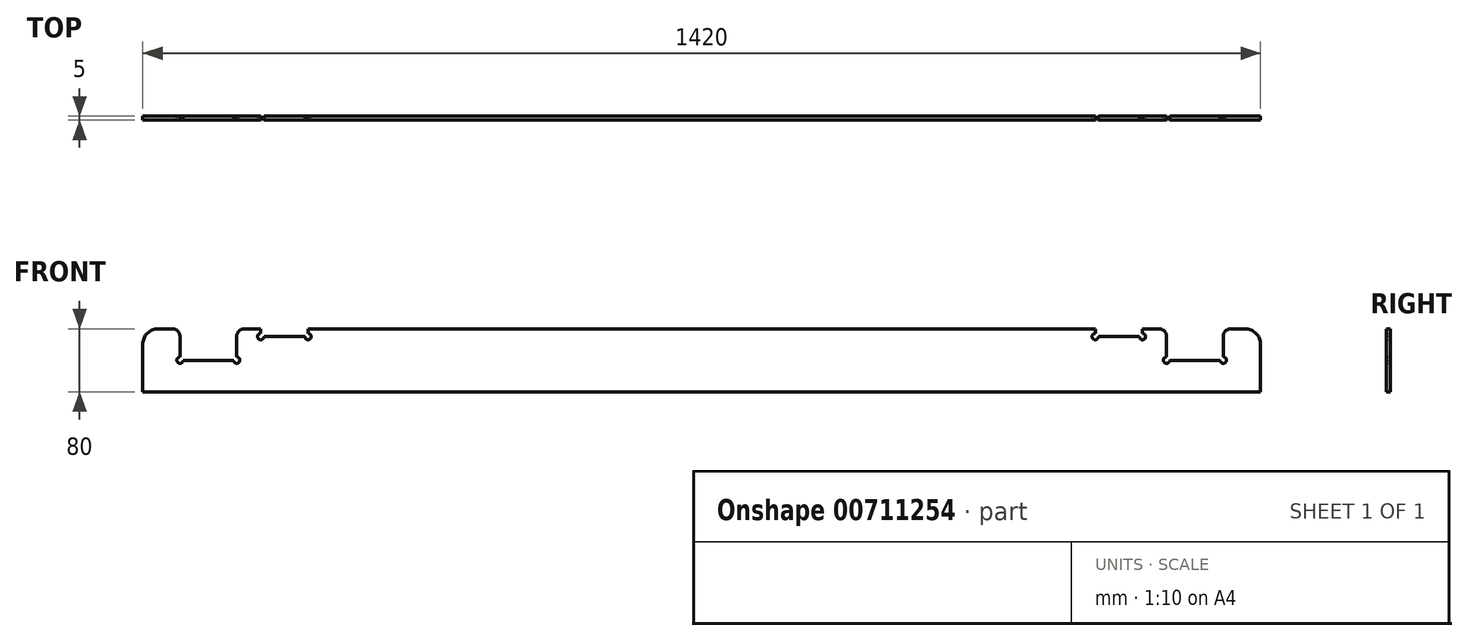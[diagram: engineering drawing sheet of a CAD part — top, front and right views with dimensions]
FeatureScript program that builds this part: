
annotation { "Feature Type Name" : "Feature", "Feature Type Description" : "" }
export const myFeature = defineFeature(function(context is Context, id is Id, definition is map)
    precondition{}
    {
        {
            var Q0;
            Q0=qCreatedBy(makeId("Front.planeOp"),FACE);
            var sketch = newSketch(context, id + "F0", { "sketchPlane" : qUnion([Q0])});
            skLineSegment(sketch, "E0.bottom", {"start": v(-690, 40) * mm, "end": v(-672.6, 40) * mm});
            skLineSegment(sketch, "E0.top", {"start": v(-710, -40) * mm, "end": v(710, -40) * mm});
            skLineSegment(sketch, "E0.left", {"start": v(-710, 20) * mm, "end": v(-710, -40) * mm});
            skLineSegment(sketch, "E0.right", {"start": v(710, 20) * mm, "end": v(710, -40) * mm});
            skPoint(sketch, "E0.middle", {"position": v(0, 0) * mm});
            skLineSegment(sketch, "E1.0", {"start": v(-560, 40) * mm, "end": v(-560, 34) * mm});
            skLineSegment(sketch, "E2.0", {"start": v(-500, 40) * mm, "end": v(-500, 34) * mm});
            skLineSegment(sketch, "E3.0", {"start": v(-556, 30) * mm, "end": v(-504, 30) * mm});
            skLineSegment(sketch, "E4.0", {"start": v(560, 40) * mm, "end": v(560, 34) * mm});
            skLineSegment(sketch, "E5.0", {"start": v(500, 40) * mm, "end": v(500, 34) * mm});
            skLineSegment(sketch, "E6.trimOffspring", {"start": v(504, 30) * mm, "end": v(556, 30) * mm});
            skLineSegment(sketch, "E7.trimOffspring", {"start": v(-500, 40) * mm, "end": v(500, 40) * mm});
            skLineSegment(sketch, "E8.trimOffspring", {"start": v(560, 40) * mm, "end": v(580.6, 40) * mm});
            skPoint(sketch, "E9.visualSharp", {"position": v(-710, 40) * mm});
            skArc(sketch, "E9.filletArc", {"start": v(-690, 40) * mm, "mid": v(-704.14, 34.14) * mm, "end": v(-710, 20) * mm});
            skArc(sketch, "E10", {"start": v(-560, 34) * mm, "mid": v(-562.83, 27.17) * mm, "end": v(-556, 30) * mm});
            skArc(sketch, "E11", {"start": v(-504, 30) * mm, "mid": v(-497.17, 27.17) * mm, "end": v(-500, 34) * mm});
            skArc(sketch, "E12", {"start": v(556, 30) * mm, "mid": v(562.83, 27.17) * mm, "end": v(560, 34) * mm});
            skArc(sketch, "E13", {"start": v(500, 34) * mm, "mid": v(497.17, 27.17) * mm, "end": v(504, 30) * mm});
            skPoint(sketch, "E14.visualSharp", {"position": v(710, 40) * mm});
            skArc(sketch, "E14.filletArc", {"start": v(710, 20) * mm, "mid": v(704.14, 34.14) * mm, "end": v(690, 40) * mm});
            skLineSegment(sketch, "E15.0", {"start": v(-662.6, 30) * mm, "end": v(-662.6, 4) * mm});
            skLineSegment(sketch, "E16.0", {"start": v(-590.6, 30) * mm, "end": v(-590.6, 4) * mm});
            skLineSegment(sketch, "E17.0", {"start": v(-658.6, 0) * mm, "end": v(-594.6, 0) * mm});
            skArc(sketch, "E18", {"start": v(-662.6, 4) * mm, "mid": v(-665.44, -2.83) * mm, "end": v(-658.6, 0) * mm});
            skArc(sketch, "E19", {"start": v(-594.6, 0) * mm, "mid": v(-587.78, -2.83) * mm, "end": v(-590.6, 4) * mm});
            skLineSegment(sketch, "E20.trimOffspring", {"start": v(-580.6, 40) * mm, "end": v(-560, 40) * mm});
            skLineSegment(sketch, "E21.MirrorCS", {"start": v(662.6, 30) * mm, "end": v(662.6, 4) * mm});
            skLineSegment(sketch, "E22.MirrorCS", {"start": v(590.6, 30) * mm, "end": v(590.6, 4) * mm});
            skLineSegment(sketch, "E23.MirrorCS", {"start": v(658.6, 0) * mm, "end": v(594.6, 0) * mm});
            skArc(sketch, "E24.MirrorCS", {"start": v(594.6, 0) * mm, "mid": v(587.78, -2.83) * mm, "end": v(590.6, 4) * mm});
            skArc(sketch, "E25.MirrorCS", {"start": v(662.6, 4) * mm, "mid": v(665.44, -2.83) * mm, "end": v(658.6, 0) * mm});
            skLineSegment(sketch, "E26.trimOffspring", {"start": v(672.6, 40) * mm, "end": v(690, 40) * mm});
            skPoint(sketch, "E27.visualSharp", {"position": v(590.6, 40) * mm});
            skArc(sketch, "E27.filletArc", {"start": v(590.6, 30) * mm, "mid": v(587.68, 37.07) * mm, "end": v(580.6, 40) * mm});
            skPoint(sketch, "E28.visualSharp", {"position": v(662.6, 40) * mm});
            skArc(sketch, "E28.filletArc", {"start": v(672.6, 40) * mm, "mid": v(665.54, 37.07) * mm, "end": v(662.6, 30) * mm});
            skPoint(sketch, "E29.visualSharp", {"position": v(-662.6, 40) * mm});
            skArc(sketch, "E29.filletArc", {"start": v(-662.6, 30) * mm, "mid": v(-665.54, 37.07) * mm, "end": v(-672.6, 40) * mm});
            skPoint(sketch, "E30.visualSharp", {"position": v(-590.6, 40) * mm});
            skArc(sketch, "E30.filletArc", {"start": v(-580.6, 40) * mm, "mid": v(-587.68, 37.07) * mm, "end": v(-590.6, 30) * mm});
            skSolve(sketch);
        }
        {
            var Q0;
            Q0=makeQuery(id+"F0.imprint","IMPRINT",FACE,{"disambiguationData":[TD([[makeQuery(id+"F0.imprint","IMPRINT",EDGE,{"derivedFrom":sQuery(id+"F0.wireOp",EDGE,"E0.bottom")}),-1.0]])]});
            extrude(context, id + "F1", {"entities" : qUnion([Q0]), "depth" : 5 * mm, "offsetDistance" : 25 * mm});
        }
    });
